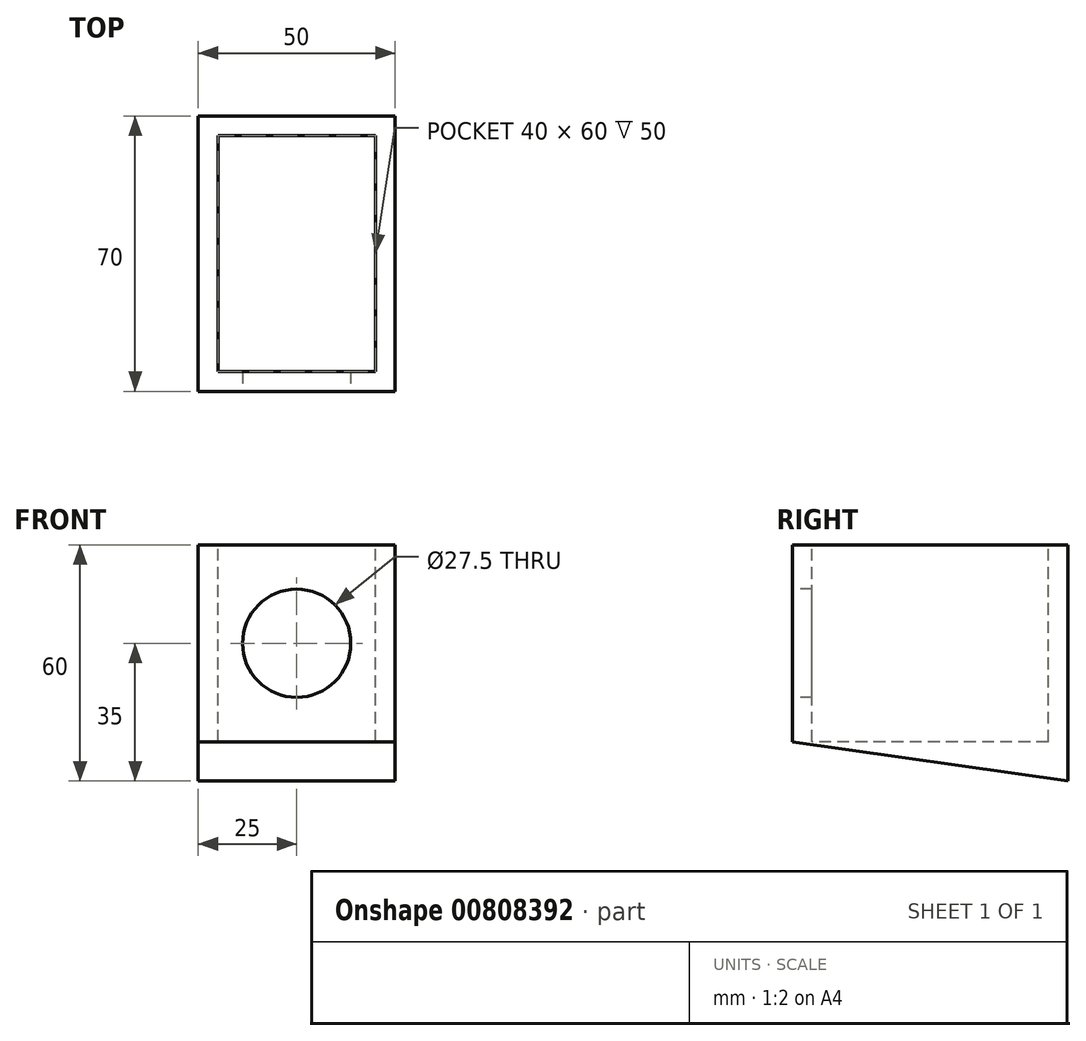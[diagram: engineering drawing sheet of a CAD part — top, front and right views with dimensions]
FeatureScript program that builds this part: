
annotation { "Feature Type Name" : "Feature", "Feature Type Description" : "" }
export const myFeature = defineFeature(function(context is Context, id is Id, definition is map)
    precondition{}
    {
        {
            var Q0;
            Q0=qCreatedBy(makeId("Front.planeOp"),FACE);
            var sketch = newSketch(context, id + "F0", { "sketchPlane" : qUnion([Q0])});
            skLineSegment(sketch, "E0.bottom", {"start": v(-25, 25) * mm, "end": v(25, 25) * mm});
            skLineSegment(sketch, "E0.top", {"start": v(-25, -25) * mm, "end": v(25, -25) * mm});
            skLineSegment(sketch, "E0.left", {"start": v(-25, 25) * mm, "end": v(-25, -25) * mm});
            skLineSegment(sketch, "E0.right", {"start": v(25, 25) * mm, "end": v(25, -25) * mm});
            skSolve(sketch);
        }
        {
            var Q0;
            Q0=qCreatedBy(makeId("Front.planeOp"),FACE);
            cPlane(context, id + "F1", {"entities" : qUnion([Q0]), "cplaneType" : CPlaneType.OFFSET, "offset" : 70 * mm, "oppositeDirection" : true, "width" : 152.4 * mm, "height" : 152.4 * mm});
        }
        {
            var Q0;
            Q0=qCreatedBy(id+"F1.planeOp",FACE);
            var sketch = newSketch(context, id + "F2", { "sketchPlane" : qUnion([Q0])});
            skLineSegment(sketch, "E1.bottom", {"start": v(25, 25) * mm, "end": v(-25, 25) * mm});
            skLineSegment(sketch, "E1.top", {"start": v(25, -35) * mm, "end": v(-25, -35) * mm});
            skLineSegment(sketch, "E1.left", {"start": v(25, 25) * mm, "end": v(25, -35) * mm});
            skLineSegment(sketch, "E1.right", {"start": v(-25, 25) * mm, "end": v(-25, -35) * mm});
            skSolve(sketch);
        }
        {
            var Q0;
            Q0=makeQuery(id+"F2.imprint","IMPRINT",FACE,{"disambiguationData":[TD([[makeQuery(id+"F2.imprint","IMPRINT",EDGE,{"derivedFrom":sQuery(id+"F2.wireOp",EDGE,"E1.bottom")}),1.0]])]});
            var Q1;
            Q1=makeQuery(id+"F0.imprint","IMPRINT",FACE,{"disambiguationData":[TD([[makeQuery(id+"F0.imprint","IMPRINT",EDGE,{"derivedFrom":sQuery(id+"F0.wireOp",EDGE,"E0.bottom")}),-1.0]])]});
            loft(context, id + "F3", {"sheetProfilesArray" : [{ "sheetProfileEntities" : qUnion([Q0]) }, { "sheetProfileEntities" : qUnion([Q1]) }]});
        }
        {
            var Q0;
            Q0=makeQuery(id+"F3.opLoft","SWEPT_FACE",FACE,{"disambiguationData":[OSD([sQuery(id+"F0.wireOp",EDGE,"E0.bottom"),sQuery(id+"F0.wireOp",EDGE,"E0.left"),sQuery(id+"F0.wireOp",EDGE,"E0.right"),sQuery(id+"F2.wireOp",EDGE,"E1.bottom"),sQuery(id+"F2.wireOp",EDGE,"E1.left"),sQuery(id+"F2.wireOp",EDGE,"E1.right")])]});
            var sketch = newSketch(context, id + "F4", { "sketchPlane" : qUnion([Q0])});
            skLineSegment(sketch, "E2.bottom", {"start": v(-20, 65) * mm, "end": v(20, 65) * mm});
            skLineSegment(sketch, "E2.top", {"start": v(-20, 5) * mm, "end": v(20, 5) * mm});
            skLineSegment(sketch, "E2.left", {"start": v(-20, 65) * mm, "end": v(-20, 5) * mm});
            skLineSegment(sketch, "E2.right", {"start": v(20, 65) * mm, "end": v(20, 5) * mm});
            skSolve(sketch);
        }
        {
            var Q0;
            Q0=makeQuery(id+"F4.imprint","IMPRINT",FACE,{"disambiguationData":[TD([[makeQuery(id+"F4.imprint","IMPRINT",EDGE,{"derivedFrom":sQuery(id+"F4.wireOp",EDGE,"E2.bottom")}),-1.0]])]});
            extrude(context, id + "F5", {"entities" : qUnion([Q0]), "operationType" : NewBodyOperationType.REMOVE, "oppositeDirection" : true, "depth" : 50 * mm, "offsetDistance" : 25.4 * mm});
        }
        {
            var Q0;
            Q0=makeQuery(id+"F3.opLoft","CAP_FACE",FACE,{"disambiguationData":[OSD([makeQuery(id+"F0.imprint","IMPRINT",FACE,{"disambiguationData":[TD([[makeQuery(id+"F0.imprint","IMPRINT",EDGE,{"derivedFrom":sQuery(id+"F0.wireOp",EDGE,"E0.bottom")}),-1.0]])]})])],"isStart":true});
            var sketch = newSketch(context, id + "F6", { "sketchPlane" : qUnion([Q0])});
            skCircle(sketch, "E3", {"center": v(0, 0) * mm, "radius": 13.75 * mm});
            skSolve(sketch);
        }
        {
            var Q0;
            Q0=makeQuery(id+"F6.imprint","IMPRINT",FACE,{"disambiguationData":[TD([[makeQuery(id+"F6.imprint","IMPRINT",EDGE,{"derivedFrom":sQuery(id+"F6.wireOp",EDGE,"E3")}),1.0]])]});
            extrude(context, id + "F7", {"entities" : qUnion([Q0]), "operationType" : NewBodyOperationType.REMOVE, "oppositeDirection" : true, "depth" : 25.4 * mm, "offsetDistance" : 25.4 * mm});
        }
    });
